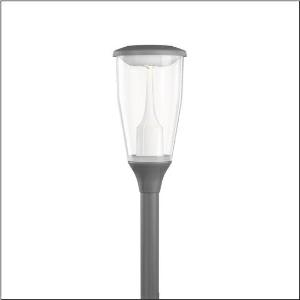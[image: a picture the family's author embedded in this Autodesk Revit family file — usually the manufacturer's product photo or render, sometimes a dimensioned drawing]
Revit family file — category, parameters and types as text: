
# Revit family: dl_11_iq___st1_2a_5xa5575mf14h000022_93a8
name_source: partatom
category: Lighting Fixtures
units: mm (PartAtom-declared; Revit-internal decimal feet)

## family parameters
Cut with Voids When Loaded = No
Host = Face
Light Source = No
Part Type = Normal
Room Calculation Point = No
Round Connector Dimension = Use Diameter
Shared = No

## types (1)
- --- (1 x LED, 1560 lm, 11.8 W, 2700K)
    Apparent Load = 12 VA
    CIE Flux Codes = 24 63 94 96 100
    Color Rendering = 70
    Color Temperature = 2700K
    Default Elevation = 1800 mm
    Description = DL 11 iQ, mast luminaire, Module 540 iQ-SR, primary light control with 3 zone facetted reflector, of plastic, silver coated, highly specular, structured, primary optical cover: cover, of PMMA, transparent, light distribution: ST1.2a, light emission: direct distribution, primary light characteristic: asymmetric, installation type: post-top, LED, High Power LED, rated luminous flux: 1.560lm, luminous efficacy: 149lm/W, light colour: 727, colour temperature: 2700K, control: Street-Remote, Auto-Match, Temp-Guard, Lumen-Switch, Night-Set, Smart-Wire, Light-Fading, Desk-Remote (wireless, voltage-free reading and setting of iQ features in the workshop via application-optimized NFC function/RFID function), optimised constant luminous flux control (CLO 2.0), mains connection: 220..240V, AC, 50/60Hz, connection cable pre-assembled, cable length: 5,5m, wiring characteristics: H07RN-F, 5-core, 1.5mm², start of lifetime: 12W, end of service life: 12W, reduction: 5W, luminaire housing, upper part, of diecast aluminium, coated, Siteco® metallic grey (DB 702S), spigot size: 76mm (post-top), post-top mast mounting element, of diecast aluminium, coated, Siteco® metallic grey (DB 702S), Module 540 iQ-SR, traffic white (RAL 9016), equipment: standard, protection rating (complete): IP66, insulation class (complete): insulation class II (safety insulation), certification: CE, ENEC, ENEC+, VDE, packaging unit: 1 piece

Light Distribution: ST1.2a
    Height = 665 mm
    Lamp = 1 x LED
    Lamp Light Flux = 1560 lm
    Lamp Power = 11.8 W
    Lamp count = 1
    Length = 334 mm
    Luminous efficacy = 132 lm/W
    Manufacturer = Siteco
    ModVariant = No
    Model = 5XA5575MF14H000022
    Number of Poles = 1
    OnlyDefault = Yes
    Power Factor = 1
    Product Name = DL 11 iQ | ST1.2a
    Product group = mast luminaire | pylon top
    ProductGroupID = 6100
    Protection Class = Protection class II
    Protection Degree = IP 66
    RLX_Detail_Level = 1
    RLX_Emergency_Light_Flux = 0 lm
    RLX_Emergency_Type = 0
    RLX_Emergency_Type_DB = No
    RlxData = <blob elided: 152381 chars, md5=3602118b>
    Socket = socket
    Standby Power = 0 W
    System Light Flux = 1560 lm
    System Power = 12 W
    Type Comments = factory setting: luminous flux: 100 % | dim-lin: 254 | 472 mA
    Type Image = l_1258354.jpg
    URL = http://relux.com
    VarID = @adj_043867
    Voltage = 0 V
    Weight = 0.00 kg
    Width = 0 mm  [stored 0 ft]

note: [stored X ft] marks values corroborated as IEEE doubles in the binary element streams (Revit-internal decimal feet)

## geometry (parser evidence)
native form markers: Blend x4, Sweep x12
no freeform markers — native parametric forms only
